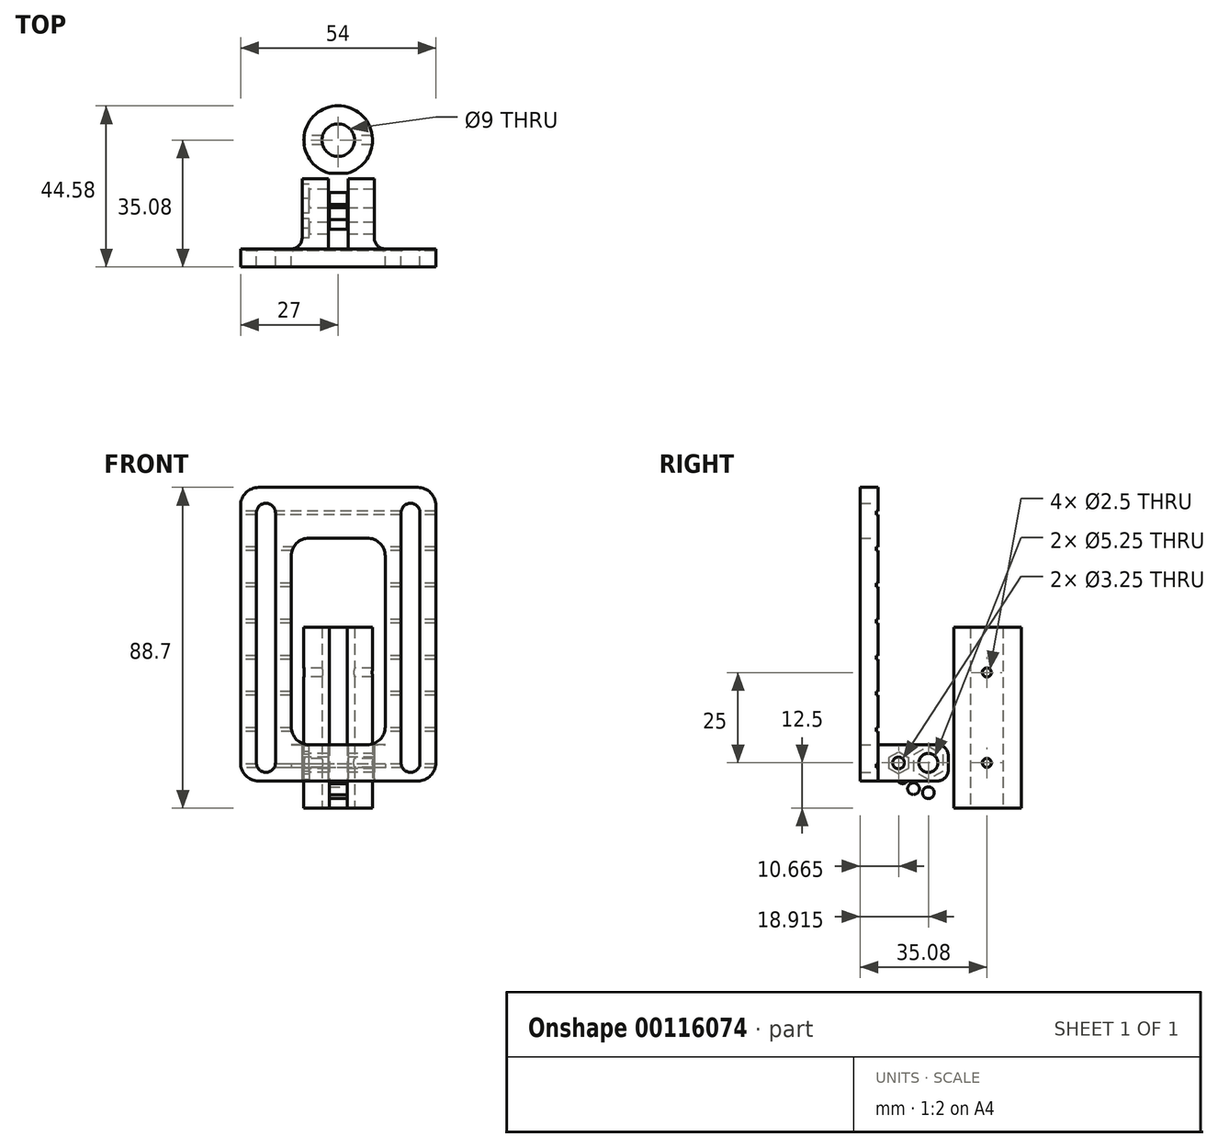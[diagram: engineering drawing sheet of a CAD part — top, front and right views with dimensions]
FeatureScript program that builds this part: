
annotation { "Feature Type Name" : "Feature", "Feature Type Description" : "" }
export const myFeature = defineFeature(function(context is Context, id is Id, definition is map)
    precondition{}
    {
        {
            var Q0;
            Q0=qCreatedBy(makeId("Top.planeOp"),FACE);
            var sketch = newSketch(context, id + "F0", { "sketchPlane" : qUnion([Q0])});
            skCircle(sketch, "E0", {"center": v(0, 0) * mm, "radius": 4.5 * mm});
            skLineSegment(sketch, "E1", {"start": v(-2.5, -28.67) * mm, "end": v(2.5, -28.67) * mm});
            skPoint(sketch, "E2.orphan", {"position": v(0, -9.5) * mm});
            skLineSegment(sketch, "E3", {"start": v(0, 0) * mm, "end": v(0, -32.6) * mm, "construction": true});
            skLineSegment(sketch, "E4", {"start": v(-2.5, -28.67) * mm, "end": v(-2.5, -9.17) * mm});
            skCircle(sketch, "E5.converted", {"center": v(0, 0) * mm, "radius": 9.5 * mm});
            skPoint(sketch, "E6.orphan", {"position": v(-9.5, 0) * mm});
            skLineSegment(sketch, "E7", {"start": v(2.5, -28.67) * mm, "end": v(2.5, -9.17) * mm});
            skLineSegment(sketch, "E8", {"start": v(2.5, -12.17) * mm, "end": v(-2.5, -12.17) * mm, "construction": true});
            skLineSegment(sketch, "E9", {"start": v(2.5, -13.67) * mm, "end": v(-2.5, -13.67) * mm, "construction": true});
            skLineSegment(sketch, "E10", {"start": v(2.5, -18.67) * mm, "end": v(-2.5, -18.67) * mm, "construction": true});
            skLineSegment(sketch, "E11", {"start": v(2.5, -20.17) * mm, "end": v(-2.5, -20.17) * mm, "construction": true});
            skLineSegment(sketch, "E12", {"start": v(2.5, -21.67) * mm, "end": v(-2.5, -21.67) * mm, "construction": true});
            skLineSegment(sketch, "E13", {"start": v(2.5, -22.92) * mm, "end": v(-2.5, -22.92) * mm, "construction": true});
            skLineSegment(sketch, "E14", {"start": v(2.5, -25.92) * mm, "end": v(-2.5, -25.92) * mm, "construction": true});
            skLineSegment(sketch, "E15", {"start": v(2.5, -27.17) * mm, "end": v(-2.5, -27.17) * mm, "construction": true});
            skLineSegment(sketch, "E16", {"start": v(3.72, -16.17) * mm, "end": v(-3.9, -16.17) * mm, "construction": true});
            skLineSegment(sketch, "E17", {"start": v(3.72, -24.42) * mm, "end": v(-3.9, -24.42) * mm, "construction": true});
            skSolve(sketch);
        }
        {
            var Q0;
            Q0=makeQuery(id+"F0.imprint","IMPRINT",FACE,{"disambiguationData":[TD([[makeQuery(id+"F0.imprint","IMPRINT",EDGE,{"derivedFrom":sQuery(id+"F0.wireOp",EDGE,"E0")}),-1.0]])]});
            var Q1;
            {var subQ4=sQuery(id+"F0.wireOp",EDGE,"E1");Q1=makeQuery(id+"F0.imprint","IMPRINT",FACE,{"disambiguationData":[TD([[makeQuery(id+"F0.imprint","IMPRINT",EDGE,{"derivedFrom":subQ4}),1.0]])]});}
            var Q2;
            {var subQ1=sQuery(id+"F0.wireOp",EDGE,"ihBdN56N-20tA-iLVV-vy9R-20qquDwyMNr0");var subQ3=sQuery(id+"F0.wireOp",EDGE,"Z5dJUpQx-MC6l-e44H-BjSD-m4GYq8Jz9UPd");var subQ4=makeQuery(id+"F0.imprint","INTERSECT",VERTEX,{"derivedFrom":[subQ1,subQ3]});Q2=makeQuery(id+"F0.imprint","IMPRINT",FACE,{"disambiguationData":[TD([[makeQuery(id+"F0.imprint","IMPRINT",EDGE,{"disambiguationData":[TD([[subQ4,-1.0]])],"derivedFrom":subQ3}),1.0]])]});}
            extrude(context, id + "F1", {"entities" : qUnion([Q0, Q1, Q2]), "depth" : 50 * mm});
        }
        {
            var Q0;
            Q0=qCreatedBy(makeId("Right.planeOp"),FACE);
            var sketch = newSketch(context, id + "F2", { "sketchPlane" : qUnion([Q0])});
            skCircle(sketch, "E18", {"center": v(0, 12.5) * mm, "radius": 1.25 * mm});
            skCircle(sketch, "E19", {"center": v(0, 37.5) * mm, "radius": 1.25 * mm});
            skSolve(sketch);
        }
        {
            var Q0;
            Q0=qSketchRegion(id+"F2",true);
            extrude(context, id + "F3", {"entities" : qUnion([Q0]), "operationType" : NewBodyOperationType.REMOVE, "endBound" : BoundingType.SYMMETRIC, "depth" : 25 * mm});
        }
        {
            var Q0;
            Q0=qCreatedBy(makeId("Right.planeOp"),FACE);
            var sketch = newSketch(context, id + "F4", { "sketchPlane" : qUnion([Q0])});
            skLineSegment(sketch, "E20", {"start": v(-24.42, 0) * mm, "end": v(-24.42, 55.12) * mm, "construction": true});
            skLineSegment(sketch, "E21", {"start": v(-16.17, 53.72) * mm, "end": v(-16.17, 0) * mm, "construction": true});
            skLineSegment(sketch, "E22.0", {"start": v(-28.67, 50) * mm, "end": v(-28.67, 0) * mm});
            skPoint(sketch, "E23.endSnap0", {"position": v(-28.67, 12.5) * mm});
            skCircle(sketch, "E24", {"center": v(-16.17, 12.5) * mm, "radius": 2.62 * mm});
            skCircle(sketch, "E25", {"center": v(-24.42, 12.5) * mm, "radius": 1.63 * mm});
            skCircle(sketch, "E26", {"center": v(-24.42, 12.5) * mm, "radius": 2.75 * mm, "construction": true});
            skCircle(sketch, "E27", {"center": v(-16.17, 12.5) * mm, "radius": 4 * mm, "construction": true});
            skPoint(sketch, "E28.center", {"position": v(-9.17, 12.5) * mm});
            skLineSegment(sketch, "E28.anchor1", {"start": v(-9.17, 12.5) * mm, "end": v(-24.42, 12.5) * mm, "construction": true});
            skLineSegment(sketch, "E29.0.0", {"start": v(-28.67, 0) * mm, "end": v(-9.17, 0) * mm});
            skLineSegment(sketch, "E29.0.1", {"start": v(-9.17, 0) * mm, "end": v(-9.17, 50) * mm});
            skLineSegment(sketch, "E29.0.2", {"start": v(-9.17, 50) * mm, "end": v(-28.67, 50) * mm});
            skCircle(sketch, "E30.1.0", {"center": v(-23.3, 16.63) * mm, "radius": 1.63 * mm});
            skCircle(sketch, "E30.1.1", {"center": v(-23.3, 16.63) * mm, "radius": 2.75 * mm, "construction": true});
            skCircle(sketch, "E30.2.0", {"center": v(-20.3, 19.64) * mm, "radius": 1.63 * mm});
            skCircle(sketch, "E30.2.1", {"center": v(-20.3, 19.64) * mm, "radius": 2.75 * mm, "construction": true});
            skCircle(sketch, "E30.3.0", {"center": v(-16.17, 20.75) * mm, "radius": 1.63 * mm});
            skCircle(sketch, "E30.3.1", {"center": v(-16.17, 20.75) * mm, "radius": 2.75 * mm, "construction": true});
            skLineSegment(sketch, "E30.anchor1", {"start": v(-16.17, 12.5) * mm, "end": v(-24.42, 12.5) * mm, "construction": true});
            skLineSegment(sketch, "E30.anchor2", {"start": v(-16.17, 12.5) * mm, "end": v(-16.17, 20.75) * mm, "construction": true});
            skCircle(sketch, "E31.MirrorC", {"center": v(-16.17, 4.25) * mm, "radius": 1.63 * mm});
            skCircle(sketch, "E32.MirrorC", {"center": v(-16.17, 4.25) * mm, "radius": 2.75 * mm, "construction": true});
            skCircle(sketch, "E33.MirrorC", {"center": v(-20.3, 5.36) * mm, "radius": 1.63 * mm});
            skCircle(sketch, "E34.MirrorC", {"center": v(-20.3, 5.36) * mm, "radius": 2.75 * mm, "construction": true});
            skCircle(sketch, "E35.MirrorC", {"center": v(-23.3, 8.38) * mm, "radius": 1.63 * mm});
            skCircle(sketch, "E36.MirrorC", {"center": v(-23.3, 8.38) * mm, "radius": 2.75 * mm, "construction": true});
            skArc(sketch, "E37", {"start": v(-16.17, 25) * mm, "mid": v(-28.67, 12.5) * mm, "end": v(-16.17, 0) * mm});
            skLineSegment(sketch, "E38", {"start": v(-16.17, 25) * mm, "end": v(-9.17, 25) * mm});
            skSolve(sketch);
        }
        {
            var Q0;
            Q0=makeQuery(id+"F4.imprint","IMPRINT",FACE,{"disambiguationData":[TD([[makeQuery(id+"F4.imprint","IMPRINT",EDGE,{"derivedFrom":sQuery(id+"F4.wireOp",EDGE,"E30.3.0")}),1.0]])]});
            var Q1;
            Q1=makeQuery(id+"F4.imprint","IMPRINT",FACE,{"disambiguationData":[TD([[makeQuery(id+"F4.imprint","IMPRINT",EDGE,{"derivedFrom":sQuery(id+"F4.wireOp",EDGE,"E30.2.0")}),1.0]])]});
            var Q2;
            Q2=makeQuery(id+"F4.imprint","IMPRINT",FACE,{"disambiguationData":[TD([[makeQuery(id+"F4.imprint","IMPRINT",EDGE,{"derivedFrom":sQuery(id+"F4.wireOp",EDGE,"E30.1.0")}),1.0]])]});
            var Q3;
            Q3=makeQuery(id+"F4.imprint","IMPRINT",FACE,{"disambiguationData":[TD([[makeQuery(id+"F4.imprint","IMPRINT",EDGE,{"derivedFrom":sQuery(id+"F4.wireOp",EDGE,"E25")}),1.0]])]});
            var Q4;
            Q4=makeQuery(id+"F4.imprint","IMPRINT",FACE,{"disambiguationData":[TD([[makeQuery(id+"F4.imprint","IMPRINT",EDGE,{"derivedFrom":sQuery(id+"F4.wireOp",EDGE,"E35.MirrorC")}),-1.0]])]});
            var Q5;
            Q5=makeQuery(id+"F4.imprint","IMPRINT",FACE,{"disambiguationData":[TD([[makeQuery(id+"F4.imprint","IMPRINT",EDGE,{"derivedFrom":sQuery(id+"F4.wireOp",EDGE,"E24")}),1.0]])]});
            var Q6;
            Q6=makeQuery(id+"F4.imprint","IMPRINT",FACE,{"disambiguationData":[TD([[makeQuery(id+"F4.imprint","IMPRINT",EDGE,{"derivedFrom":sQuery(id+"F4.wireOp",EDGE,"E33.MirrorC")}),-1.0]])]});
            var Q7;
            Q7=makeQuery(id+"F4.imprint","IMPRINT",FACE,{"disambiguationData":[TD([[makeQuery(id+"F4.imprint","IMPRINT",EDGE,{"derivedFrom":sQuery(id+"F4.wireOp",EDGE,"E31.MirrorC")}),-1.0]])]});
            var Q8;
            {var subQ0=sQuery(id+"F4.wireOp",EDGE,"E22.0");var subQ1=sQuery(id+"F4.wireOp",EDGE,"E29.0.0");var subQ2=makeQuery(id+"F4.imprint","INTERSECT",VERTEX,{"derivedFrom":[subQ1,subQ0]});Q8=makeQuery(id+"F4.imprint","IMPRINT",FACE,{"disambiguationData":[TD([[makeQuery(id+"F4.imprint","IMPRINT",EDGE,{"disambiguationData":[TD([[subQ2,-1.0]])],"derivedFrom":subQ1}),1.0]])]});}
            var Q9;
            {var subQ1=sQuery(id+"F4.wireOp",EDGE,"E29.0.2");Q9=makeQuery(id+"F4.imprint","IMPRINT",FACE,{"disambiguationData":[TD([[makeQuery(id+"F4.imprint","IMPRINT",EDGE,{"derivedFrom":subQ1}),1.0]])]});}
            extrude(context, id + "F5", {"entities" : qUnion([Q0, Q1, Q2, Q3, Q4, Q5, Q6, Q7, Q8, Q9]), "operationType" : NewBodyOperationType.REMOVE, "endBound" : BoundingType.THROUGH_ALL, "oppositeDirection" : true, "depth" : 25 * mm, "hasSecondDirection" : true, "secondDirectionBound" : SecondDirectionBoundingType.THROUGH_ALL, "secondDirectionOppositeDirection" : false, "secondDirectionDepth" : 25 * mm});
        }
        {
            var Q0;
            Q0=qCreatedBy(makeId("Right.planeOp"),FACE);
            var sketch = newSketch(context, id + "F6", { "sketchPlane" : qUnion([Q0])});
            skCircle(sketch, "E39.0", {"center": v(-16.17, 12.5) * mm, "radius": 2.62 * mm});
            skCircle(sketch, "E40.0", {"center": v(-24.42, 12.5) * mm, "radius": 1.63 * mm});
            skLineSegment(sketch, "E41", {"start": v(-16.17, 12.5) * mm, "end": v(-24.42, 12.5) * mm, "construction": true});
            skLineSegment(sketch, "E42.bottom", {"start": v(-13.67, 17.5) * mm, "end": v(-30.08, 17.5) * mm});
            skLineSegment(sketch, "E42.top", {"start": v(-13.67, 7.5) * mm, "end": v(-30.08, 7.5) * mm});
            skLineSegment(sketch, "E42.left", {"start": v(-10.67, 14.5) * mm, "end": v(-10.67, 10.5) * mm});
            skLineSegment(sketch, "E42.right", {"start": v(-30.08, 17.5) * mm, "end": v(-30.08, 7.5) * mm});
            skLineSegment(sketch, "E43.0", {"start": v(-9.17, 25) * mm, "end": v(-9.17, 0) * mm});
            skCircle(sketch, "E44.cCircle", {"center": v(-16.17, 12.5) * mm, "radius": 4 * mm, "construction": true});
            skLineSegment(sketch, "E44.0", {"start": v(-20.17, 14.8) * mm, "end": v(-16.17, 17.12) * mm});
            skLineSegment(sketch, "E44.1", {"start": v(-16.17, 17.12) * mm, "end": v(-12.17, 14.8) * mm});
            skLineSegment(sketch, "E44.2", {"start": v(-12.17, 14.8) * mm, "end": v(-12.17, 10.2) * mm});
            skLineSegment(sketch, "E44.3", {"start": v(-12.17, 10.2) * mm, "end": v(-16.17, 7.88) * mm});
            skLineSegment(sketch, "E44.4", {"start": v(-16.17, 7.88) * mm, "end": v(-20.17, 10.2) * mm});
            skLineSegment(sketch, "E44.5", {"start": v(-20.17, 10.2) * mm, "end": v(-20.17, 14.8) * mm});
            skPoint(sketch, "E44.0.midPoint", {"position": v(-18.17, 15.96) * mm});
            skCircle(sketch, "E45.cCircle", {"center": v(-24.42, 12.5) * mm, "radius": 2.66 * mm, "construction": true});
            skLineSegment(sketch, "E45.0", {"start": v(-27.08, 14.04) * mm, "end": v(-24.42, 15.57) * mm});
            skLineSegment(sketch, "E45.1", {"start": v(-24.42, 15.57) * mm, "end": v(-21.76, 14.04) * mm});
            skLineSegment(sketch, "E45.2", {"start": v(-21.76, 14.04) * mm, "end": v(-21.76, 10.96) * mm});
            skLineSegment(sketch, "E45.3", {"start": v(-21.76, 10.96) * mm, "end": v(-24.42, 9.43) * mm});
            skLineSegment(sketch, "E45.4", {"start": v(-24.42, 9.43) * mm, "end": v(-27.08, 10.96) * mm});
            skLineSegment(sketch, "E45.5", {"start": v(-27.08, 10.96) * mm, "end": v(-27.08, 14.04) * mm});
            skPoint(sketch, "E45.0.midPoint", {"position": v(-25.75, 14.8) * mm});
            skPoint(sketch, "E46.visualSharp", {"position": v(-10.67, 17.5) * mm});
            skArc(sketch, "E46.filletArc", {"start": v(-10.67, 14.5) * mm, "mid": v(-11.54, 16.62) * mm, "end": v(-13.67, 17.5) * mm});
            skPoint(sketch, "E47.visualSharp", {"position": v(-10.67, 7.5) * mm});
            skArc(sketch, "E47.filletArc", {"start": v(-13.67, 7.5) * mm, "mid": v(-11.54, 8.38) * mm, "end": v(-10.67, 10.5) * mm});
            skSolve(sketch);
        }
        {
            var Q0;
            Q0=makeQuery(id+"F6.imprint","IMPRINT",FACE,{"disambiguationData":[TD([[makeQuery(id+"F6.imprint","IMPRINT",EDGE,{"derivedFrom":sQuery(id+"F6.wireOp",EDGE,"E42.bottom")}),1.0]])]});
            extrude(context, id + "F7", {"entities" : qUnion([Q0]), "endBound" : BoundingType.SYMMETRIC, "depth" : 20 * mm});
        }
        {
            var Q0;
            Q0=makeQuery(id+"F6.imprint","IMPRINT",FACE,{"disambiguationData":[TD([[makeQuery(id+"F6.imprint","IMPRINT",EDGE,{"derivedFrom":sQuery(id+"F6.wireOp",EDGE,"E39.0")}),-1.0]])]});
            var Q1;
            Q1=makeQuery(id+"F6.imprint","IMPRINT",FACE,{"disambiguationData":[TD([[makeQuery(id+"F6.imprint","IMPRINT",EDGE,{"derivedFrom":sQuery(id+"F6.wireOp",EDGE,"E40.0")}),-1.0]])]});
            var Q2;
            Q2=makeQuery(id+"F7.opExtrude","CAP_FACE",FACE,{"disambiguationData":[OSD([sQuery(id+"F6.wireOp",EDGE,"E42.bottom"),sQuery(id+"F6.wireOp",EDGE,"E42.top"),sQuery(id+"F6.wireOp",EDGE,"E42.left"),sQuery(id+"F6.wireOp",EDGE,"E42.right"),sQuery(id+"F6.wireOp",EDGE,"E44.0"),sQuery(id+"F6.wireOp",EDGE,"E44.1"),sQuery(id+"F6.wireOp",EDGE,"E44.2"),sQuery(id+"F6.wireOp",EDGE,"E44.3"),sQuery(id+"F6.wireOp",EDGE,"E44.4"),sQuery(id+"F6.wireOp",EDGE,"E44.5"),sQuery(id+"F6.wireOp",EDGE,"E45.0"),sQuery(id+"F6.wireOp",EDGE,"E45.1"),sQuery(id+"F6.wireOp",EDGE,"E45.2"),sQuery(id+"F6.wireOp",EDGE,"E45.3"),sQuery(id+"F6.wireOp",EDGE,"E45.4"),sQuery(id+"F6.wireOp",EDGE,"E45.5"),sQuery(id+"F6.wireOp",EDGE,"E46.filletArc"),sQuery(id+"F6.wireOp",EDGE,"E47.filletArc")])],"isStart":false});
            extrude(context, id + "F8", {"entities" : qUnion([Q0, Q1]), "operationType" : NewBodyOperationType.ADD, "endBound" : BoundingType.UP_TO_SURFACE, "endBoundEntityFace" : qUnion([Q2]), "depth" : 16 * mm, "hasSecondDirection" : true, "secondDirectionOppositeDirection" : true, "secondDirectionDepth" : 8 * mm});
        }
        {
            var Q0;
            Q0=makeQuery(id+"F6.imprint","IMPRINT",FACE,{"disambiguationData":[TD([[makeQuery(id+"F6.imprint","IMPRINT",EDGE,{"derivedFrom":sQuery(id+"F6.wireOp",EDGE,"E42.bottom")}),1.0]])]});
            var Q1;
            Q1=makeQuery(id+"F6.imprint","IMPRINT",FACE,{"disambiguationData":[TD([[makeQuery(id+"F6.imprint","IMPRINT",EDGE,{"derivedFrom":sQuery(id+"F6.wireOp",EDGE,"E39.0")}),-1.0]])]});
            var Q2;
            Q2=makeQuery(id+"F6.imprint","IMPRINT",FACE,{"disambiguationData":[TD([[makeQuery(id+"F6.imprint","IMPRINT",EDGE,{"derivedFrom":sQuery(id+"F6.wireOp",EDGE,"E40.0")}),-1.0]])]});
            extrude(context, id + "F9", {"entities" : qUnion([Q0, Q1, Q2]), "operationType" : NewBodyOperationType.REMOVE, "endBound" : BoundingType.SYMMETRIC, "oppositeDirection" : true, "depth" : 5.5 * mm});
        }
        {
            var Q0;
            {var subQ0=sQuery(id+"F6.wireOp",EDGE,"E42.bottom");var subQ1=sQuery(id+"F6.wireOp",EDGE,"E47.filletArc");var subQ2=sQuery(id+"F6.wireOp",EDGE,"E46.filletArc");var subQ3=sQuery(id+"F6.wireOp",EDGE,"E42.right");var subQ4=sQuery(id+"F6.wireOp",EDGE,"E42.left");var subQ5=sQuery(id+"F6.wireOp",EDGE,"E42.top");Q0=makeQuery(id+"F9.boolean.opBoolean","SPLIT",FACE,{"disambiguationData":[TD([makeQuery(id+"F9.opExtrude","CAP_FACE",FACE,{"disambiguationData":[OSD([sQuery(id+"F6.wireOp",EDGE,"E39.0"),sQuery(id+"F6.wireOp",EDGE,"E40.0"),subQ0,subQ5,subQ4,subQ3,subQ2,subQ1])],"isStart":true})])],"derivedFrom":makeQuery(id+"F7.opExtrude","SWEPT_FACE",FACE,{"disambiguationData":[OSD([subQ3])]})});}
            var sketch = newSketch(context, id + "F10", { "sketchPlane" : qUnion([Q0])});
            skLineSegment(sketch, "E48.0.0", {"start": v(-2.75, 7.5) * mm, "end": v(-2.75, 17.5) * mm, "construction": true});
            skLineSegment(sketch, "E48.0.1", {"start": v(-2.75, 17.5) * mm, "end": v(-10, 17.5) * mm, "construction": true});
            skLineSegment(sketch, "E48.0.2", {"start": v(-10, 17.5) * mm, "end": v(-10, 7.5) * mm, "construction": true});
            skLineSegment(sketch, "E48.0.3", {"start": v(-10, 7.5) * mm, "end": v(-2.75, 7.5) * mm, "construction": true});
            skLineSegment(sketch, "E49.0.0", {"start": v(10, 17.5) * mm, "end": v(2.75, 17.5) * mm, "construction": true});
            skLineSegment(sketch, "E49.0.1", {"start": v(2.75, 17.5) * mm, "end": v(2.75, 7.5) * mm, "construction": true});
            skLineSegment(sketch, "E49.0.2", {"start": v(2.75, 7.5) * mm, "end": v(10, 7.5) * mm, "construction": true});
            skLineSegment(sketch, "E49.0.3", {"start": v(10, 7.5) * mm, "end": v(10, 17.5) * mm, "construction": true});
            skLineSegment(sketch, "E50", {"start": v(-10, 12.5) * mm, "end": v(10, 12.5) * mm, "construction": true});
            skLineSegment(sketch, "E51.bottom", {"start": v(-27, 7.5) * mm, "end": v(27, 7.5) * mm});
            skLineSegment(sketch, "E51.top", {"start": v(-27, 88.7) * mm, "end": v(27, 88.7) * mm});
            skLineSegment(sketch, "E51.left", {"start": v(-27, 7.5) * mm, "end": v(-27, 88.7) * mm});
            skLineSegment(sketch, "E51.right", {"start": v(27, 7.5) * mm, "end": v(27, 88.7) * mm});
            skLineSegment(sketch, "E52.bottom", {"start": v(-13, 17.5) * mm, "end": v(13, 17.5) * mm});
            skLineSegment(sketch, "E52.top", {"start": v(-13, 74.7) * mm, "end": v(13, 74.7) * mm});
            skLineSegment(sketch, "E52.left", {"start": v(-13, 17.5) * mm, "end": v(-13, 74.7) * mm});
            skLineSegment(sketch, "E52.right", {"start": v(13, 17.5) * mm, "end": v(13, 74.7) * mm});
            skLineSegment(sketch, "E53", {"start": v(0, 12.5) * mm, "end": v(0, 59.66) * mm, "construction": true});
            skPoint(sketch, "E53.endSnap0", {"position": v(0, 12.5) * mm});
            skArc(sketch, "E54", {"start": v(-17.38, 81.7) * mm, "mid": v(-20, 84.33) * mm, "end": v(-22.63, 81.7) * mm});
            skArc(sketch, "E55", {"start": v(-22.63, 12.5) * mm, "mid": v(-20, 9.88) * mm, "end": v(-17.38, 12.5) * mm});
            skLineSegment(sketch, "E56", {"start": v(-22.63, 12.5) * mm, "end": v(-22.63, 81.7) * mm});
            skLineSegment(sketch, "E57", {"start": v(-17.38, 81.7) * mm, "end": v(-17.38, 12.5) * mm});
            skArc(sketch, "E58.MirrorCS", {"start": v(22.63, 12.5) * mm, "mid": v(20, 9.88) * mm, "end": v(17.38, 12.5) * mm});
            skLineSegment(sketch, "E59.MirrorCS", {"start": v(22.63, 12.5) * mm, "end": v(22.63, 81.7) * mm});
            skLineSegment(sketch, "E60.MirrorCS", {"start": v(17.38, 81.7) * mm, "end": v(17.38, 12.5) * mm});
            skArc(sketch, "E61.MirrorCS", {"start": v(17.37, 81.7) * mm, "mid": v(20, 84.33) * mm, "end": v(22.62, 81.7) * mm});
            skSolve(sketch);
        }
        {
            var Q0;
            Q0 = qSketchRegion(id + "F10", true);
            extrude(context, id + "F11", {"entities" : qUnion([Q0]), "operationType" : NewBodyOperationType.ADD, "depth" : 5 * mm});
        }
        {
            var Q0;
            Q0=makeQuery(id+"F11.opExtrude","SWEPT_EDGE",EDGE,{"disambiguationData":[OSD([sQuery(id+"F10.wireOp",EDGE,"E51.top"),sQuery(id+"F10.wireOp",EDGE,"E51.left")])]});
            var Q1;
            Q1=makeQuery(id+"F11.opExtrude","SWEPT_EDGE",EDGE,{"disambiguationData":[OSD([sQuery(id+"F10.wireOp",EDGE,"E51.bottom"),sQuery(id+"F10.wireOp",EDGE,"E51.left")])]});
            var Q2;
            Q2=makeQuery(id+"F11.opExtrude","SWEPT_EDGE",EDGE,{"disambiguationData":[OSD([sQuery(id+"F10.wireOp",EDGE,"E51.bottom"),sQuery(id+"F10.wireOp",EDGE,"E51.right")])]});
            var Q3;
            Q3=makeQuery(id+"F11.opExtrude","SWEPT_EDGE",EDGE,{"disambiguationData":[OSD([sQuery(id+"F10.wireOp",EDGE,"E51.top"),sQuery(id+"F10.wireOp",EDGE,"E51.right")])]});
            var Q4;
            Q4=makeQuery(id+"F11.opExtrude","SWEPT_EDGE",EDGE,{"disambiguationData":[OSD([sQuery(id+"F10.wireOp",EDGE,"E52.top"),sQuery(id+"F10.wireOp",EDGE,"E52.left")])]});
            var Q5;
            Q5=makeQuery(id+"F11.opExtrude","SWEPT_EDGE",EDGE,{"disambiguationData":[OSD([sQuery(id+"F10.wireOp",EDGE,"E52.bottom"),sQuery(id+"F10.wireOp",EDGE,"E52.left")])]});
            var Q6;
            Q6=makeQuery(id+"F11.opExtrude","SWEPT_EDGE",EDGE,{"disambiguationData":[OSD([sQuery(id+"F10.wireOp",EDGE,"E52.bottom"),sQuery(id+"F10.wireOp",EDGE,"E52.right")])]});
            var Q7;
            Q7=makeQuery(id+"F11.opExtrude","SWEPT_EDGE",EDGE,{"disambiguationData":[OSD([sQuery(id+"F10.wireOp",EDGE,"E52.top"),sQuery(id+"F10.wireOp",EDGE,"E52.right")])]});
            fillet(context, id + "F12", {"entities" : qUnion([Q0, Q1, Q2, Q3, Q4, Q5, Q6, Q7]), "radius" : 5 * mm, "tangentPropagation" : true, "allowEdgeOverflow" : false});
        }
        {
            var Q0;
            Q0=makeQuery(id+"F7.opExtrude","CAP_EDGE",EDGE,{"disambiguationData":[OSD([sQuery(id+"F6.wireOp",EDGE,"E42.right")])],"isStart":false});
            var Q1;
            Q1=makeQuery(id+"F7.opExtrude","CAP_EDGE",EDGE,{"disambiguationData":[OSD([sQuery(id+"F6.wireOp",EDGE,"E42.right")])],"isStart":true});
            fillet(context, id + "F13", {"entities" : qUnion([Q0, Q1]), "radius" : 3 * mm, "tangentPropagation" : true, "allowEdgeOverflow" : false});
        }
        {
            var Q0;
            {var subQ0=sQuery(id+"F10.wireOp",EDGE,"E51.bottom");var subQ1=sQuery(id+"F10.wireOp",EDGE,"E51.left");var subQ20=sQuery(id+"F10.wireOp",EDGE,"E52.right");var subQ21=sQuery(id+"F10.wireOp",EDGE,"E51.top");var subQ22=sQuery(id+"F10.wireOp",EDGE,"E52.left");var subQ23=sQuery(id+"F10.wireOp",EDGE,"E51.right");var subQ24=sQuery(id+"F10.wireOp",EDGE,"E52.bottom");var subQ25=sQuery(id+"F10.wireOp",EDGE,"E52.top");var subQ26=sQuery(id+"F10.wireOp",EDGE,"E54");var subQ27=sQuery(id+"F10.wireOp",EDGE,"E55");var subQ28=sQuery(id+"F10.wireOp",EDGE,"E56");var subQ29=sQuery(id+"F10.wireOp",EDGE,"E57");var subQ30=sQuery(id+"F10.wireOp",EDGE,"E58.MirrorCS");var subQ31=sQuery(id+"F10.wireOp",EDGE,"E59.MirrorCS");var subQ32=sQuery(id+"F10.wireOp",EDGE,"E60.MirrorCS");var subQ33=sQuery(id+"F10.wireOp",EDGE,"E61.MirrorCS");Q0=makeQuery(id+"F11.boolean.opBoolean","SPLIT",FACE,{"disambiguationData":[TD([makeQuery(id+"F11.opExtrude","SWEPT_FACE",FACE,{"disambiguationData":[OSD([subQ21])]})])],"derivedFrom":makeQuery(id+"F11.opExtrude","CAP_FACE",FACE,{"disambiguationData":[OSD([subQ0,subQ21,subQ1,subQ23,subQ24,subQ25,subQ22,subQ20,subQ26,subQ27,subQ28,subQ29,subQ30,subQ31,subQ32,subQ33])],"isStart":true})});}
            var sketch = newSketch(context, id + "F14", { "sketchPlane" : qUnion([Q0])});
            skLineSegment(sketch, "E62", {"start": v(-27, 81.7) * mm, "end": v(27, 81.7) * mm, "construction": true});
            skLineSegment(sketch, "E63.0", {"start": v(-27, 81.2) * mm, "end": v(27, 81.2) * mm});
            skLineSegment(sketch, "E64.0", {"start": v(-27, 82.2) * mm, "end": v(27, 82.2) * mm});
            skLineSegment(sketch, "E65", {"start": v(-27, 82.2) * mm, "end": v(-27, 81.2) * mm});
            skLineSegment(sketch, "E66", {"start": v(27, 82.2) * mm, "end": v(27, 81.2) * mm});
            skLineSegment(sketch, "E67.1.0.0", {"start": v(27, 72.2) * mm, "end": v(27, 71.2) * mm});
            skLineSegment(sketch, "E67.1.0.1", {"start": v(-27, 71.2) * mm, "end": v(27, 71.2) * mm});
            skLineSegment(sketch, "E67.1.0.2", {"start": v(-27, 72.2) * mm, "end": v(27, 72.2) * mm});
            skLineSegment(sketch, "E67.1.0.3", {"start": v(-27, 72.2) * mm, "end": v(-27, 71.2) * mm});
            skLineSegment(sketch, "E67.2.0.0", {"start": v(27, 62.2) * mm, "end": v(27, 61.2) * mm});
            skLineSegment(sketch, "E67.2.0.1", {"start": v(-27, 61.2) * mm, "end": v(27, 61.2) * mm});
            skLineSegment(sketch, "E67.2.0.2", {"start": v(-27, 62.2) * mm, "end": v(27, 62.2) * mm});
            skLineSegment(sketch, "E67.2.0.3", {"start": v(-27, 62.2) * mm, "end": v(-27, 61.2) * mm});
            skLineSegment(sketch, "E67.3.0.0", {"start": v(27, 52.2) * mm, "end": v(27, 51.2) * mm});
            skLineSegment(sketch, "E67.3.0.1", {"start": v(-27, 51.2) * mm, "end": v(27, 51.2) * mm});
            skLineSegment(sketch, "E67.3.0.2", {"start": v(-27, 52.2) * mm, "end": v(27, 52.2) * mm});
            skLineSegment(sketch, "E67.3.0.3", {"start": v(-27, 52.2) * mm, "end": v(-27, 51.2) * mm});
            skLineSegment(sketch, "E67.4.0.0", {"start": v(27, 42.2) * mm, "end": v(27, 41.2) * mm});
            skLineSegment(sketch, "E67.4.0.1", {"start": v(-27, 41.2) * mm, "end": v(27, 41.2) * mm});
            skLineSegment(sketch, "E67.4.0.2", {"start": v(-27, 42.2) * mm, "end": v(27, 42.2) * mm});
            skLineSegment(sketch, "E67.4.0.3", {"start": v(-27, 42.2) * mm, "end": v(-27, 41.2) * mm});
            skLineSegment(sketch, "E67.5.0.0", {"start": v(27, 32.2) * mm, "end": v(27, 31.2) * mm});
            skLineSegment(sketch, "E67.5.0.1", {"start": v(-27, 31.2) * mm, "end": v(27, 31.2) * mm});
            skLineSegment(sketch, "E67.5.0.2", {"start": v(-27, 32.2) * mm, "end": v(27, 32.2) * mm});
            skLineSegment(sketch, "E67.5.0.3", {"start": v(-27, 32.2) * mm, "end": v(-27, 31.2) * mm});
            skLineSegment(sketch, "E67.6.0.0", {"start": v(27, 22.2) * mm, "end": v(27, 21.2) * mm});
            skLineSegment(sketch, "E67.6.0.1", {"start": v(-27, 21.2) * mm, "end": v(27, 21.2) * mm});
            skLineSegment(sketch, "E67.6.0.2", {"start": v(-27, 22.2) * mm, "end": v(27, 22.2) * mm});
            skLineSegment(sketch, "E67.6.0.3", {"start": v(-27, 22.2) * mm, "end": v(-27, 21.2) * mm});
            skLineSegment(sketch, "E67.7.0.0", {"start": v(27, 12.2) * mm, "end": v(27, 11.2) * mm});
            skLineSegment(sketch, "E67.7.0.1", {"start": v(-27, 11.2) * mm, "end": v(27, 11.2) * mm});
            skLineSegment(sketch, "E67.7.0.2", {"start": v(-27, 12.2) * mm, "end": v(27, 12.2) * mm});
            skLineSegment(sketch, "E67.7.0.3", {"start": v(-27, 12.2) * mm, "end": v(-27, 11.2) * mm});
            skLineSegment(sketch, "E67.direction1", {"start": v(-27, 81.2) * mm, "end": v(-27, 71.2) * mm, "construction": true});
            skSolve(sketch);
        }
        {
            var Q0;
            Q0 = qSketchRegion(id + "F14", true);
            extrude(context, id + "F15", {"entities" : qUnion([Q0]), "operationType" : NewBodyOperationType.REMOVE, "oppositeDirection" : true, "depth" : 0.5 * mm});
        }
    });
